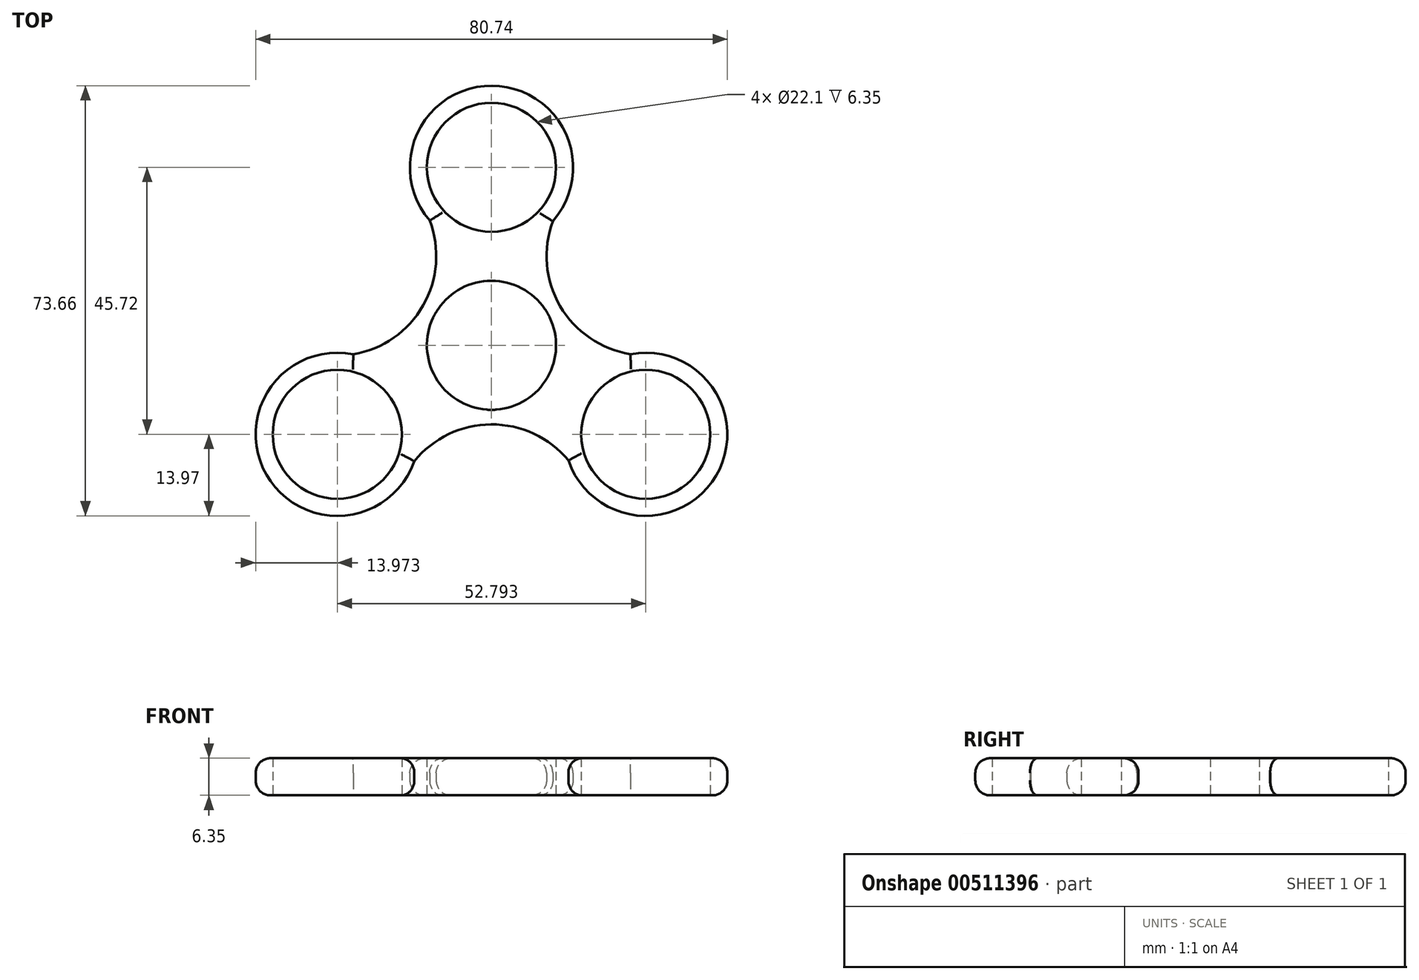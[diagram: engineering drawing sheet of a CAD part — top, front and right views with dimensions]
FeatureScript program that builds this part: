
annotation { "Feature Type Name" : "Feature", "Feature Type Description" : "" }
export const myFeature = defineFeature(function(context is Context, id is Id, definition is map)
    precondition{}
    {
        {
            var Q0;
            Q0=qCreatedBy(makeId("Top.planeOp"),FACE);
            var sketch = newSketch(context, id + "F0", { "sketchPlane" : qUnion([Q0])});
            skCircle(sketch, "E0", {"center": v(0, 0) * mm, "radius": 11.05 * mm});
            skLineSegment(sketch, "E1", {"start": v(0, 0) * mm, "end": v(0, 30.48) * mm});
            skCircle(sketch, "E2", {"center": v(0, 30.48) * mm, "radius": 11.05 * mm});
            skCircle(sketch, "E3.1.0", {"center": v(-26.4, -15.24) * mm, "radius": 11.05 * mm});
            skCircle(sketch, "E3.2.0", {"center": v(26.4, -15.24) * mm, "radius": 11.05 * mm});
            skCircle(sketch, "E4", {"center": v(0, 30.48) * mm, "radius": 13.97 * mm});
            skCircle(sketch, "E5.1.0", {"center": v(-26.4, -15.24) * mm, "radius": 13.97 * mm});
            skCircle(sketch, "E5.2.0", {"center": v(26.4, -15.24) * mm, "radius": 13.97 * mm});
            skArc(sketch, "E6", {"start": v(-23.66, -1.54) * mm, "mid": v(-11.7, 6.82) * mm, "end": v(-10.59, 21.37) * mm});
            skArc(sketch, "E7.1.0", {"start": v(13.16, -19.72) * mm, "mid": v(-0.06, -13.54) * mm, "end": v(-13.21, -19.86) * mm});
            skArc(sketch, "E7.2.0", {"start": v(10.5, 21.26) * mm, "mid": v(11.75, 6.72) * mm, "end": v(23.8, -1.51) * mm});
            skSolve(sketch);
        }
        {
            var Q0;
            Q0=makeQuery(id+"F0.imprint","IMPRINT",FACE,{"disambiguationData":[TD([[makeQuery(id+"F0.imprint","IMPRINT",EDGE,{"derivedFrom":sQuery(id+"F0.wireOp",EDGE,"E0")}),-1.0]])]});
            var Q1;
            Q1=makeQuery(id+"F0.imprint","IMPRINT",FACE,{"disambiguationData":[TD([[makeQuery(id+"F0.imprint","IMPRINT",EDGE,{"derivedFrom":sQuery(id+"F0.wireOp",EDGE,"E2")}),-1.0]])]});
            var Q2;
            Q2=makeQuery(id+"F0.imprint","IMPRINT",FACE,{"disambiguationData":[TD([[makeQuery(id+"F0.imprint","IMPRINT",EDGE,{"derivedFrom":sQuery(id+"F0.wireOp",EDGE,"E3.1.0")}),-1.0]])]});
            var Q3;
            Q3=makeQuery(id+"F0.imprint","IMPRINT",FACE,{"disambiguationData":[TD([[makeQuery(id+"F0.imprint","IMPRINT",EDGE,{"derivedFrom":sQuery(id+"F0.wireOp",EDGE,"E3.2.0")}),-1.0]])]});
            extrude(context, id + "F1", {"entities" : qUnion([Q0, Q1, Q2, Q3]), "depth" : 6.35 * mm});
        }
        {
            var Q0;
            Q0=makeQuery(id+"F1.opExtrude","CAP_EDGE",EDGE,{"disambiguationData":[OSD([sQuery(id+"F0.wireOp",EDGE,"E4")])],"isStart":false});
            var Q1;
            Q1=makeQuery(id+"F1.opExtrude","CAP_EDGE",EDGE,{"disambiguationData":[OSD([sQuery(id+"F0.wireOp",EDGE,"E6")])],"isStart":false});
            var Q2;
            Q2=makeQuery(id+"F1.opExtrude","CAP_EDGE",EDGE,{"disambiguationData":[OSD([sQuery(id+"F0.wireOp",EDGE,"E5.1.0")])],"isStart":false});
            var Q3;
            Q3=makeQuery(id+"F1.opExtrude","CAP_EDGE",EDGE,{"disambiguationData":[OSD([sQuery(id+"F0.wireOp",EDGE,"E7.1.0")])],"isStart":false});
            var Q4;
            Q4=makeQuery(id+"F1.opExtrude","CAP_EDGE",EDGE,{"disambiguationData":[OSD([sQuery(id+"F0.wireOp",EDGE,"E5.2.0")])],"isStart":false});
            var Q5;
            Q5=makeQuery(id+"F1.opExtrude","CAP_EDGE",EDGE,{"disambiguationData":[OSD([sQuery(id+"F0.wireOp",EDGE,"E7.2.0")])],"isStart":false});
            var Q6;
            Q6=makeQuery(id+"F1.opExtrude","CAP_EDGE",EDGE,{"disambiguationData":[OSD([sQuery(id+"F0.wireOp",EDGE,"E6")])],"isStart":true});
            var Q7;
            Q7=makeQuery(id+"F1.opExtrude","CAP_EDGE",EDGE,{"disambiguationData":[OSD([sQuery(id+"F0.wireOp",EDGE,"E4")])],"isStart":true});
            var Q8;
            Q8=makeQuery(id+"F1.opExtrude","CAP_EDGE",EDGE,{"disambiguationData":[OSD([sQuery(id+"F0.wireOp",EDGE,"E7.2.0")])],"isStart":true});
            var Q9;
            Q9=makeQuery(id+"F1.opExtrude","CAP_EDGE",EDGE,{"disambiguationData":[OSD([sQuery(id+"F0.wireOp",EDGE,"E5.2.0")])],"isStart":true});
            var Q10;
            Q10=makeQuery(id+"F1.opExtrude","CAP_EDGE",EDGE,{"disambiguationData":[OSD([sQuery(id+"F0.wireOp",EDGE,"E7.1.0")])],"isStart":true});
            var Q11;
            Q11=makeQuery(id+"F1.opExtrude","CAP_EDGE",EDGE,{"disambiguationData":[OSD([sQuery(id+"F0.wireOp",EDGE,"E5.1.0")])],"isStart":true});
            fillet(context, id + "F2", {"entities" : qUnion([Q0, Q1, Q2, Q3, Q4, Q5, Q6, Q7, Q8, Q9, Q10, Q11]), "radius" : 2.54 * mm, "tangentPropagation" : true, "allowEdgeOverflow" : false});
        }
    });
